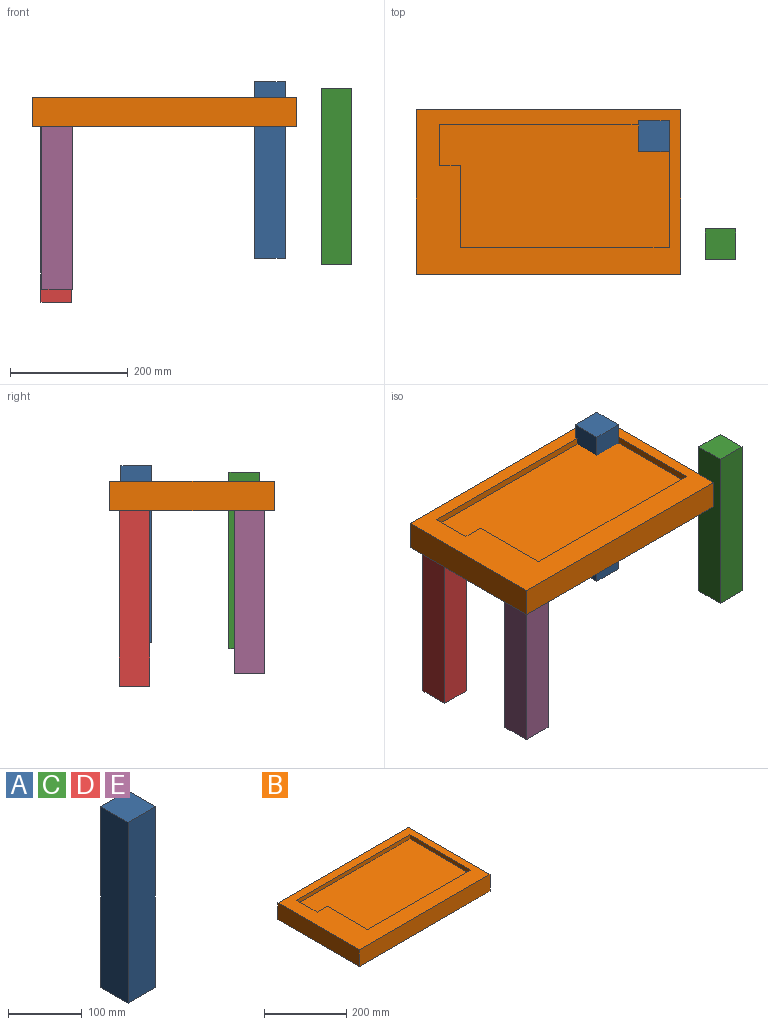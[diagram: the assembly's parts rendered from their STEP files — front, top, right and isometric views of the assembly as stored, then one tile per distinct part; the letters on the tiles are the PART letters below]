
ASSEMBLY  parts=5 mates=1
PART A: 6 faces, bbox 52x52x300 mm
  f0: plane 300x52mm, normal (-1,0,0), area 15600mm2, adj f1,f3,f4,f5
  f1: plane 300x52mm, normal (0,-1,0), area 15600mm2, adj f0,f2,f4,f5
  f2: plane 300x52mm, normal (1,0,0), area 15600mm2, adj f1,f3,f4,f5
  f3: plane 300x52mm, normal (0,1,0), area 15600mm2, adj f0,f2,f4,f5
  f4: plane 52x52mm, normal (0,0,1), area 2704mm2, adj f0,f1,f2,f3
  f5: plane 52x52mm, normal (0,0,-1), area 2704mm2, adj f0,f1,f2,f3
PART B: 33 faces, bbox 450x280x50 mm
  f0: plane 450x280mm, normal (0,0,-1), area 113900mm2, adj f2,f3,f4,f5,f13,f14,f15,f16
  f1: plane 450x280mm, normal (0,0,1), area 49000mm2, adj f2,f3,f4,f5,f6,f7,f8,f10
  f2: plane 450x50mm, normal (0,1,0), area 22500mm2, adj f0,f1,f3,f5
  f3: plane 280x50mm, normal (-1,0,0), area 14000mm2, adj f0,f1,f2,f4
  f4: plane 450x50mm, normal (0,-1,0), area 22500mm2, adj f0,f1,f3,f5
  f5: plane 280x50mm, normal (1,0,0), area 14000mm2, adj f0,f1,f2,f4
  f6: plane 390x12mm, normal (0,-1,0), area 4680mm2, adj f1,f7,f9,f11
  f7: plane 70x12mm, normal (1,0,0), area 840mm2, adj f1,f6,f8,f9
  f8: plane 35x12mm, normal (0,1,0), area 420mm2, adj f1,f7,f9,f10
  f9: plane 390x210mm, normal (0,0,1), area 77000mm2, adj f6,f7,f8,f10,f11,f12
  f10: plane 140x12mm, normal (1,0,0), area 1680mm2, adj f1,f8,f9,f12
  f11: plane 210x12mm, normal (-1,0,0), area 2520mm2, adj f1,f6,f9,f12
  f12: plane 355x12mm, normal (0,1,0), area 4260mm2, adj f1,f9,f10,f11
  f13: plane 55x23mm, normal (0,1,0), area 1265mm2, adj f0,f14,f16,f17
  f14: plane 55x23mm, normal (1,0,0), area 1265mm2, adj f0,f13,f15,f17
  f15: plane 55x23mm, normal (0,-1,0), area 1265mm2, adj f0,f14,f16,f17
  f16: plane 55x23mm, normal (-1,0,0), area 1265mm2, adj f0,f13,f15,f17
  f17: plane 55x55mm, normal (0,0,-1), area 3025mm2, adj f13,f14,f15,f16
  f18: plane 55x23mm, normal (0,1,0), area 1265mm2, adj f0,f19,f21,f22
  f19: plane 55x23mm, normal (1,0,0), area 1265mm2, adj f0,f18,f20,f22
  f20: plane 55x23mm, normal (0,-1,0), area 1265mm2, adj f0,f19,f21,f22
  f21: plane 55x23mm, normal (-1,0,0), area 1265mm2, adj f0,f18,f20,f22
  f22: plane 55x55mm, normal (0,0,-1), area 3025mm2, adj f18,f19,f20,f21
  f23: plane 55x23mm, normal (0,1,0), area 1265mm2, adj f0,f24,f26,f27
  f24: plane 55x23mm, normal (1,0,0), area 1265mm2, adj f0,f23,f25,f27
  f25: plane 55x23mm, normal (0,-1,0), area 1265mm2, adj f0,f24,f26,f27
  f26: plane 55x23mm, normal (-1,0,0), area 1265mm2, adj f0,f23,f25,f27
  f27: plane 55x55mm, normal (0,0,-1), area 3025mm2, adj f23,f24,f25,f26
  f28: plane 55x23mm, normal (0,1,0), area 1265mm2, adj f0,f29,f31,f32
  f29: plane 55x23mm, normal (1,0,0), area 1265mm2, adj f0,f28,f30,f32
  f30: plane 55x23mm, normal (0,-1,0), area 1265mm2, adj f0,f29,f31,f32
  f31: plane 55x23mm, normal (-1,0,0), area 1265mm2, adj f0,f28,f30,f32
  f32: plane 55x55mm, normal (0,0,-1), area 3025mm2, adj f28,f29,f30,f31
PART C: same geometry as A
PART D: same geometry as A
PART E: same geometry as A
PLACE A t=(77.46,54.18,-328.45)mm
PLACE B t=(-33.37,9.45,-104.4)mm
PLACE C t=(190.81,-129.46,-339.44)mm
PLACE D t=(-285.74,57.27,-402.78)mm
PLACE E t=(-284.21,-138.1,-381.4)mm
MATE fastened E.f4 <-> B.f17  axis (0,0,1) through (-276.61,-133.56,-81.4)mm
